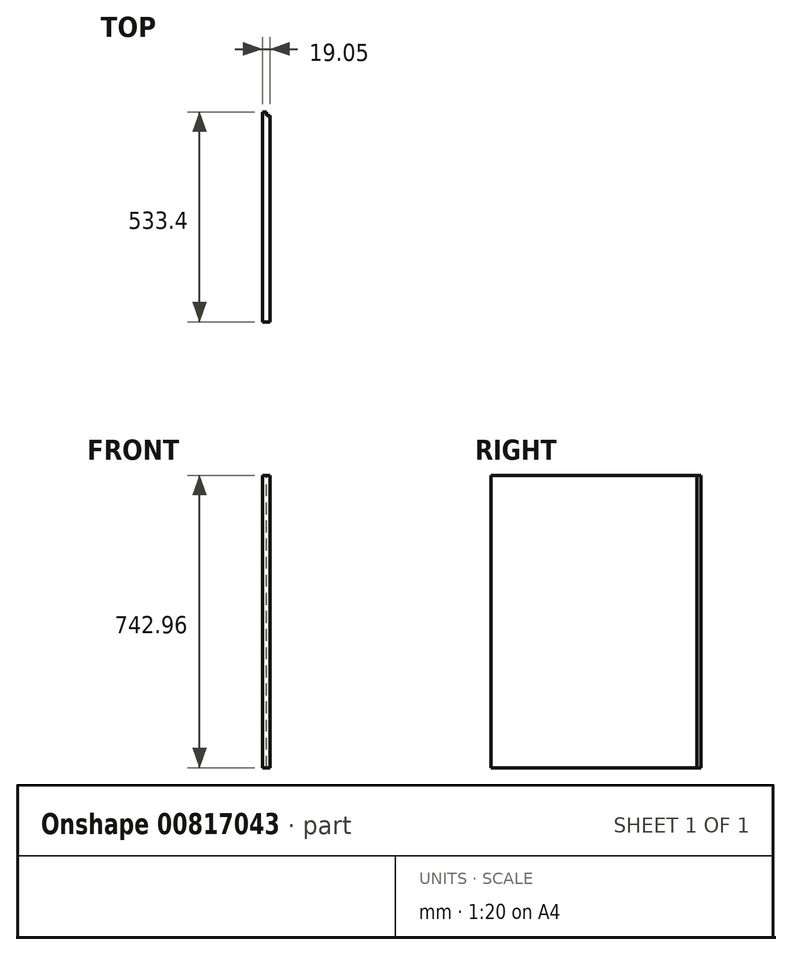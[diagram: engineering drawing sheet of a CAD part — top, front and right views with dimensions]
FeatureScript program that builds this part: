
annotation { "Feature Type Name" : "Feature", "Feature Type Description" : "" }
export const myFeature = defineFeature(function(context is Context, id is Id, definition is map)
    precondition{}
    {
        {
            var Q0;
            Q0=qCreatedBy(makeId("Right.planeOp"),FACE);
            var sketch = newSketch(context, id + "F0", { "sketchPlane" : qUnion([Q0])});
            skLineSegment(sketch, "E0.bottom", {"start": v(266.7, 371.48) * mm, "end": v(-266.7, 371.48) * mm});
            skLineSegment(sketch, "E0.top", {"start": v(266.7, -371.48) * mm, "end": v(-266.7, -371.48) * mm});
            skLineSegment(sketch, "E0.left", {"start": v(266.7, 371.48) * mm, "end": v(266.7, -371.48) * mm});
            skLineSegment(sketch, "E0.right", {"start": v(-266.7, 371.48) * mm, "end": v(-266.7, -371.48) * mm});
            skPoint(sketch, "E0.middle", {"position": v(0, 0) * mm});
            skSolve(sketch);
        }
        {
            var Q0;
            Q0 = qSketchRegion(id + "F0", true);
            extrude(context, id + "F1", {"entities" : qUnion([Q0]), "depth" : 19.05 * mm, "offsetDistance" : 25.4 * mm});
        }
        {
            var Q0;
            Q0=makeQuery(id+"F1.opExtrude","SWEPT_FACE",FACE,{"disambiguationData":[OSD([sQuery(id+"F0.wireOp",EDGE,"E0.bottom")])]});
            var sketch = newSketch(context, id + "F2", { "sketchPlane" : qUnion([Q0])});
            skLineSegment(sketch, "E1.bottom", {"start": v(19.05, 266.7) * mm, "end": v(9.53, 266.7) * mm});
            skLineSegment(sketch, "E1.top", {"start": v(19.05, 257.18) * mm, "end": v(9.53, 257.18) * mm});
            skLineSegment(sketch, "E1.left", {"start": v(19.05, 266.7) * mm, "end": v(19.05, 257.18) * mm});
            skLineSegment(sketch, "E1.right", {"start": v(9.53, 266.7) * mm, "end": v(9.53, 257.18) * mm});
            skSolve(sketch);
        }
        {
            var Q0;
            Q0 = qSketchRegion(id + "F2", true);
            var Q1;
            Q1=makeQuery(id+"F1.opExtrude","SWEPT_FACE",FACE,{"disambiguationData":[OSD([sQuery(id+"F0.wireOp",EDGE,"E0.top")])]});
            extrude(context, id + "F3", {"entities" : qUnion([Q0]), "operationType" : NewBodyOperationType.REMOVE, "endBound" : BoundingType.UP_TO_SURFACE, "oppositeDirection" : true, "depth" : 25.4 * mm, "endBoundEntityFace" : qUnion([Q1]), "offsetDistance" : 25.4 * mm});
        }
    });
